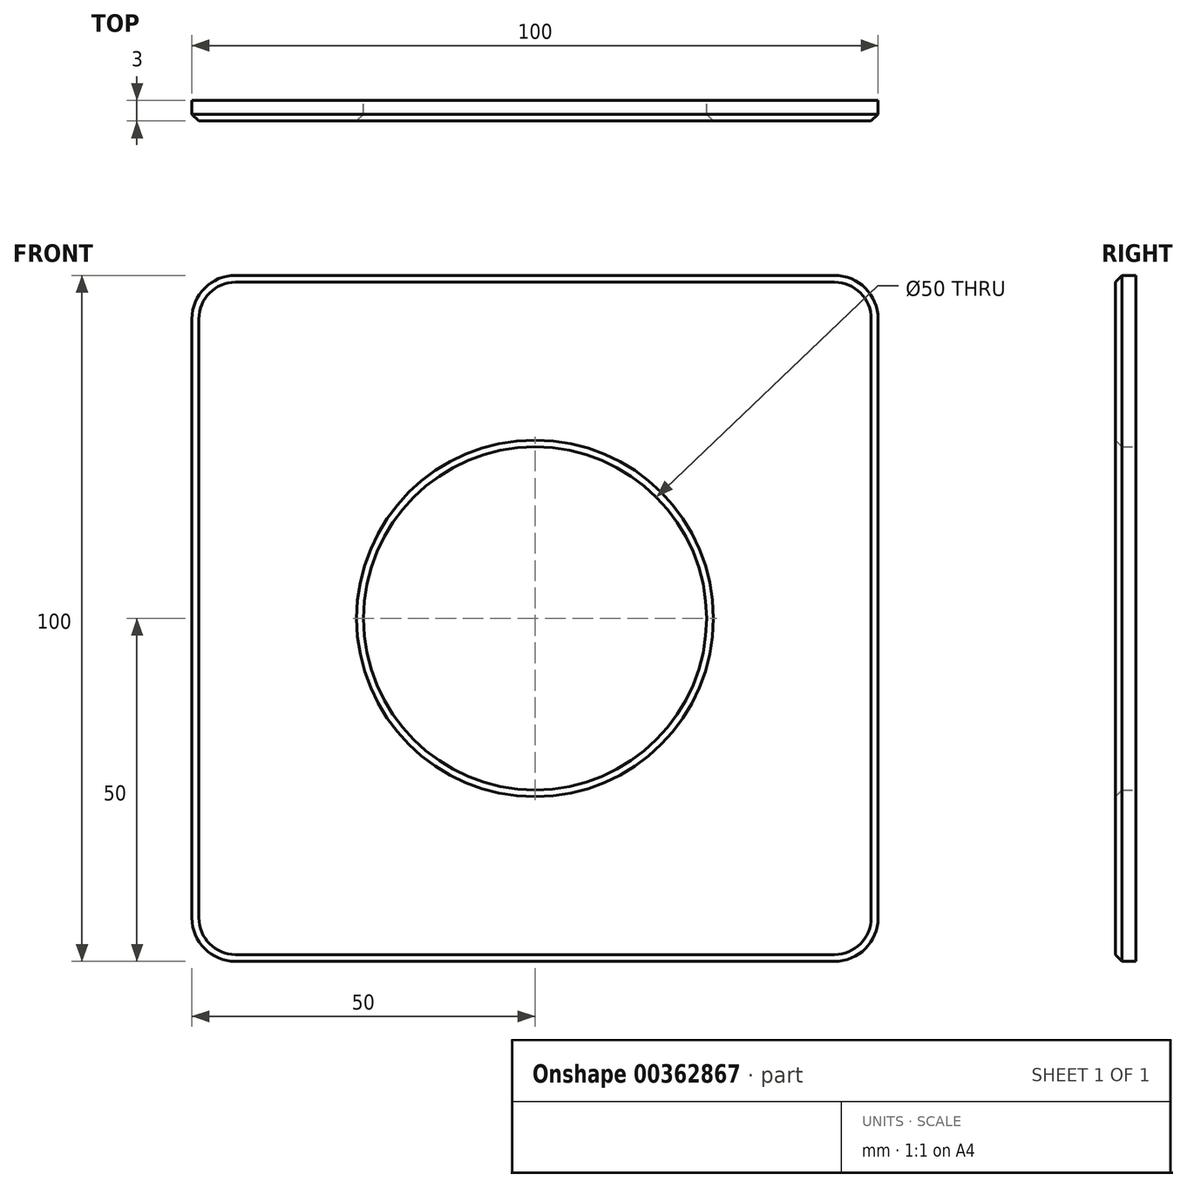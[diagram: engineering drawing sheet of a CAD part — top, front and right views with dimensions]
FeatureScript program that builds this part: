
annotation { "Feature Type Name" : "Feature", "Feature Type Description" : "" }
export const myFeature = defineFeature(function(context is Context, id is Id, definition is map)
    precondition{}
    {
        {
            var Q0;
            Q0=qCreatedBy(makeId("Front.planeOp"),FACE);
            var sketch = newSketch(context, id + "F0", { "sketchPlane" : qUnion([Q0])});
            skLineSegment(sketch, "E0.bottom", {"start": v(-43.65, 50) * mm, "end": v(43.65, 50) * mm});
            skLineSegment(sketch, "E0.top", {"start": v(-43.65, -50) * mm, "end": v(43.65, -50) * mm});
            skLineSegment(sketch, "E0.left", {"start": v(-50, 43.65) * mm, "end": v(-50, -43.65) * mm});
            skLineSegment(sketch, "E0.right", {"start": v(50, 43.65) * mm, "end": v(50, -43.65) * mm});
            skPoint(sketch, "E0.middle", {"position": v(0, 0) * mm});
            skPoint(sketch, "E1.visualSharp", {"position": v(-50, 50) * mm});
            skArc(sketch, "E1.filletArc", {"start": v(-43.65, 50) * mm, "mid": v(-48.14, 48.14) * mm, "end": v(-50, 43.65) * mm});
            skPoint(sketch, "E2.visualSharp", {"position": v(50, 50) * mm});
            skArc(sketch, "E2.filletArc", {"start": v(50, 43.65) * mm, "mid": v(48.14, 48.14) * mm, "end": v(43.65, 50) * mm});
            skPoint(sketch, "E3.visualSharp", {"position": v(50, -50) * mm});
            skArc(sketch, "E3.filletArc", {"start": v(43.65, -50) * mm, "mid": v(48.14, -48.14) * mm, "end": v(50, -43.65) * mm});
            skPoint(sketch, "E4.visualSharp", {"position": v(-50, -50) * mm});
            skArc(sketch, "E4.filletArc", {"start": v(-50, -43.65) * mm, "mid": v(-48.14, -48.14) * mm, "end": v(-43.65, -50) * mm});
            skCircle(sketch, "E5", {"center": v(0, 0) * mm, "radius": 25 * mm});
            skSolve(sketch);
        }
        {
            var Q0;
            Q0=makeQuery(id+"F0.imprint","IMPRINT",FACE,{"disambiguationData":[TD([[makeQuery(id+"F0.imprint","IMPRINT",EDGE,{"derivedFrom":sQuery(id+"F0.wireOp",EDGE,"E0.bottom")}),-1.0]])]});
            extrude(context, id + "F1", {"entities" : qUnion([Q0]), "depth" : 3 * mm});
        }
        {
            var Q0;
            Q0=makeQuery(id+"F1.opExtrude","CAP_FACE",FACE,{"disambiguationData":[OSD([sQuery(id+"F0.wireOp",EDGE,"E0.bottom"),sQuery(id+"F0.wireOp",EDGE,"E0.top"),sQuery(id+"F0.wireOp",EDGE,"E0.left"),sQuery(id+"F0.wireOp",EDGE,"E0.right"),sQuery(id+"F0.wireOp",EDGE,"E1.filletArc"),sQuery(id+"F0.wireOp",EDGE,"E2.filletArc"),sQuery(id+"F0.wireOp",EDGE,"E3.filletArc"),sQuery(id+"F0.wireOp",EDGE,"E4.filletArc"),sQuery(id+"F0.wireOp",EDGE,"E5")])],"isStart":false});
            chamfer(context, id + "F2", {"entities" : qUnion([Q0]), "width" : 1 * mm, "tangentPropagation" : true});
        }
    });
